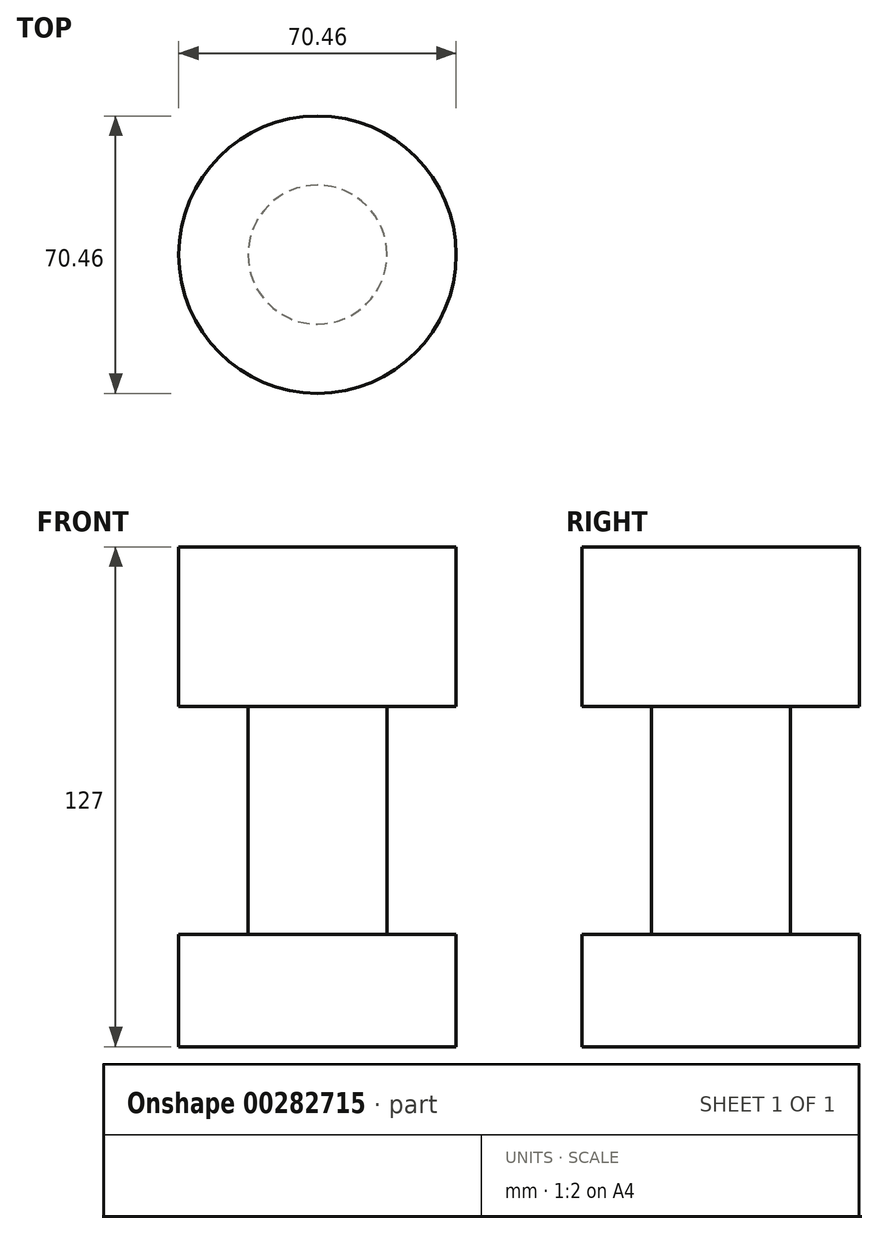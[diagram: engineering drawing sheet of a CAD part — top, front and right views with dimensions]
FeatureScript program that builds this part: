
annotation { "Feature Type Name" : "Feature", "Feature Type Description" : "" }
export const myFeature = defineFeature(function(context is Context, id is Id, definition is map)
    precondition{}
    {
        {
            var Q0;
            Q0=qCreatedBy(makeId("Top.planeOp"),FACE);
            var sketch = newSketch(context, id + "F0", { "sketchPlane" : qUnion([Q0])});
            skCircle(sketch, "E0", {"center": v(0, 0) * mm, "radius": 35.23 * mm});
            skSolve(sketch);
        }
        {
            var Q0;
            Q0 = qSketchRegion(id + "F0", true);
            extrude(context, id + "F1", {"entities" : qUnion([Q0]), "depth" : 127 * mm});
        }
        {
            var Q0;
            Q0=qCreatedBy(makeId("Right.planeOp"),FACE);
            var sketch = newSketch(context, id + "F2", { "sketchPlane" : qUnion([Q0])});
            skLineSegment(sketch, "E1.bottom", {"start": v(-35.3, 86.41) * mm, "end": v(-17.65, 86.41) * mm});
            skLineSegment(sketch, "E1.top", {"start": v(-35.3, 28.47) * mm, "end": v(-17.65, 28.47) * mm});
            skLineSegment(sketch, "E1.left", {"start": v(-35.3, 86.41) * mm, "end": v(-35.3, 28.47) * mm});
            skLineSegment(sketch, "E1.right", {"start": v(-17.65, 86.41) * mm, "end": v(-17.65, 28.47) * mm});
            skSolve(sketch);
        }
        {
            var Q0;
            Q0=qCreatedBy(makeId("Right.planeOp"),FACE);
            var sketch = newSketch(context, id + "F3", { "sketchPlane" : qUnion([Q0])});
            skLineSegment(sketch, "E2", {"start": v(0, 0) * mm, "end": v(0, 101) * mm, "construction": true});
            skSolve(sketch);
        }
        {
            var Q0;
            Q0=makeQuery(id+"F2.imprint","IMPRINT",FACE,{"disambiguationData":[TD([[makeQuery(id+"F2.imprint","IMPRINT",EDGE,{"derivedFrom":sQuery(id+"F2.wireOp",EDGE,"E1.bottom")}),-1.0]])]});
            var Q1;
            Q1=sQuery(id+"F3.wireOp",EDGE,"E2");
            var Q2;
            Q2=sQuery(id+"F3.wireOp",EDGE,"E2");
            revolve(context, id + "F4", {"operationType" : NewBodyOperationType.REMOVE, "entities" : qUnion([Q0]), "surfaceEntities" : qUnion([Q1]), "axis" : qUnion([Q2]), "revolveType" : RevolveType.FULL, "oppositeDirection" : true});
        }
    });
